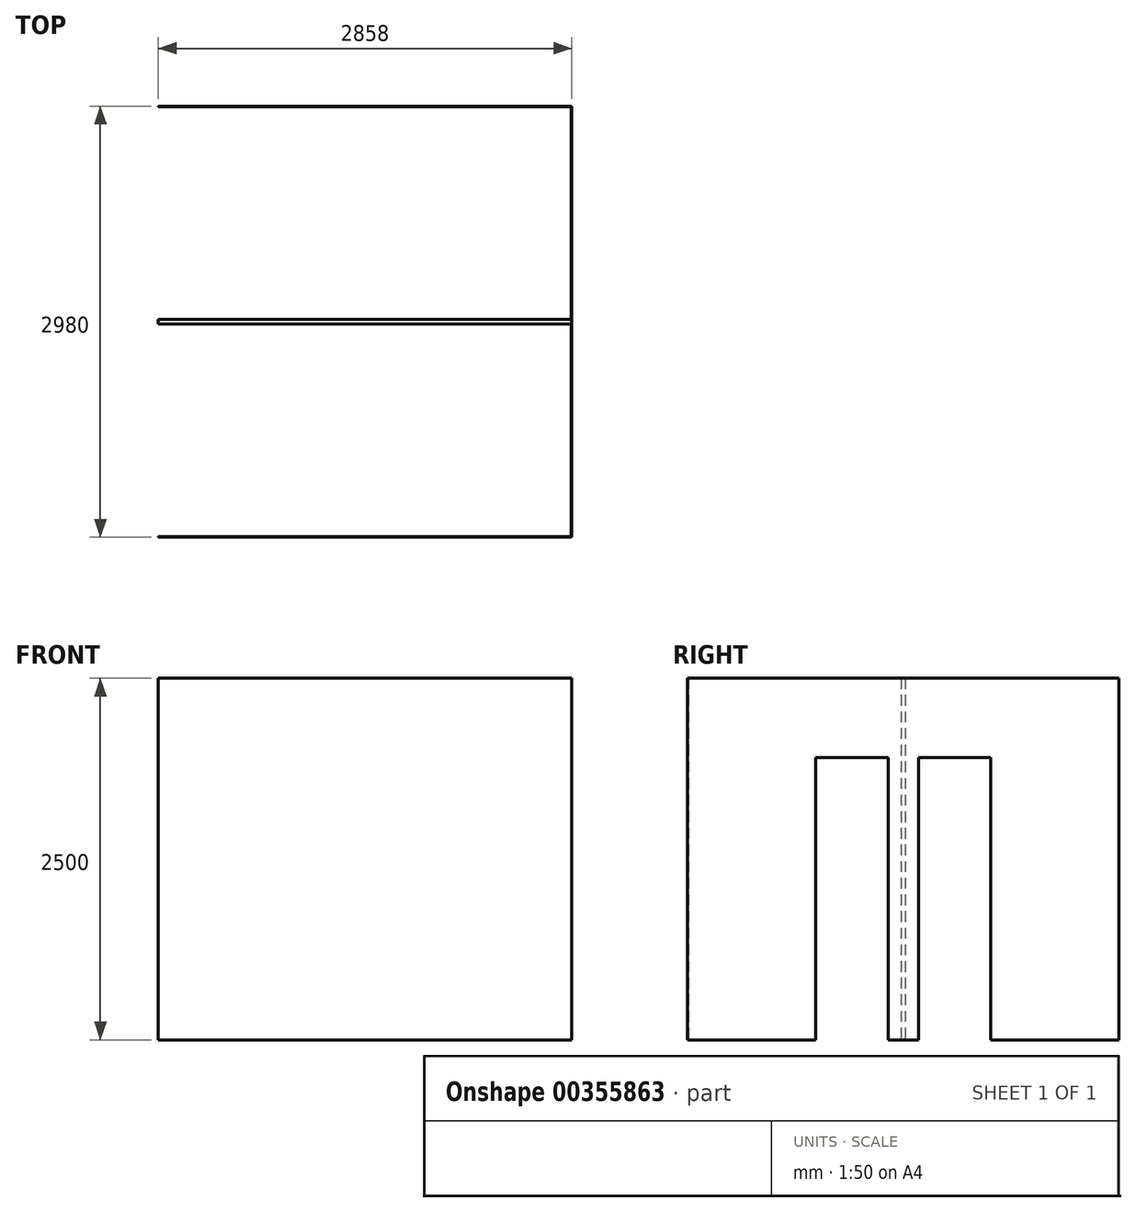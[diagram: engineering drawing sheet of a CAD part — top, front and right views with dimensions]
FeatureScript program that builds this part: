
annotation { "Feature Type Name" : "Feature", "Feature Type Description" : "" }
export const myFeature = defineFeature(function(context is Context, id is Id, definition is map)
    precondition{}
    {
        {
            var Q0;
            Q0=qCreatedBy(makeId("Top.planeOp"),FACE);
            var sketch = newSketch(context, id + "F0", { "sketchPlane" : qUnion([Q0])});
            skLineSegment(sketch, "E0.top", {"start": v(8302.06, 5858.21) * mm, "end": v(5348.06, 5858.21) * mm});
            skLineSegment(sketch, "E1.trimOffspring", {"start": v(8302.06, 8838.21) * mm, "end": v(8302.06, 7358.21) * mm});
            skPoint(sketch, "E2.start.orphan", {"position": v(8302.06, 7348.21) * mm});
            skLineSegment(sketch, "E3.trimOffspring", {"start": v(8302.06, 7338.21) * mm, "end": v(8302.06, 5858.21) * mm});
            skPoint(sketch, "E4.orphan", {"position": v(5348.06, 8858.21) * mm});
            skPoint(sketch, "E5.orphan", {"position": v(5348.06, 8838.21) * mm});
            skLineSegment(sketch, "E6", {"start": v(8302.06, 8838.21) * mm, "end": v(5348.06, 8838.21) * mm});
            skPoint(sketch, "E7.orphan", {"position": v(5348.06, 5858.21) * mm});
            skLineSegment(sketch, "E8.0", {"start": v(8297.06, 8833.21) * mm, "end": v(5348.06, 8833.21) * mm});
            skLineSegment(sketch, "E8.1", {"start": v(8297.06, 8833.21) * mm, "end": v(8297.06, 7363.21) * mm});
            skLineSegment(sketch, "E8.2", {"start": v(8297.06, 7363.21) * mm, "end": v(5343.06, 7363.21) * mm});
            skLineSegment(sketch, "E8.3", {"start": v(8297.06, 5863.21) * mm, "end": v(5348.06, 5863.21) * mm});
            skLineSegment(sketch, "E8.4", {"start": v(8297.06, 7333.21) * mm, "end": v(8297.06, 5863.21) * mm});
            skLineSegment(sketch, "E8.5", {"start": v(8297.06, 7333.21) * mm, "end": v(5343.06, 7333.21) * mm});
            skLineSegment(sketch, "E8.6", {"start": v(5343.06, 7363.21) * mm, "end": v(5343.06, 7333.21) * mm});
            skLineSegment(sketch, "E9", {"start": v(5348.06, 8833.21) * mm, "end": v(5348.06, 8838.21) * mm});
            skLineSegment(sketch, "E10", {"start": v(5348.06, 5863.21) * mm, "end": v(5348.06, 5858.21) * mm});
            skLineSegment(sketch, "E11", {"start": v(8302.06, 7358.21) * mm, "end": v(8302.06, 7338.21) * mm});
            skSolve(sketch);
        }
        {
            var Q0;
            Q0=qSketchRegion(id+"F0",true);
            extrude(context, id + "F1", {"entities" : qUnion([Q0]), "depth" : 2500 * mm});
        }
        {
            var Q0;
            Q0=makeQuery(id+"F1.opExtrude","SWEPT_FACE",FACE,{"disambiguationData":[OSD([sQuery(id+"F0.wireOp",EDGE,"E8.1")])]});
            var sketch = newSketch(context, id + "F2", { "sketchPlane" : qUnion([Q0])});
            skLineSegment(sketch, "E12.bottom", {"start": v(-7453.21, 1950) * mm, "end": v(-7953.21, 1950) * mm});
            skLineSegment(sketch, "E12.top", {"start": v(-7453.21, 0) * mm, "end": v(-7953.21, 0) * mm});
            skLineSegment(sketch, "E12.left", {"start": v(-7453.21, 1950) * mm, "end": v(-7453.21, 0) * mm});
            skLineSegment(sketch, "E12.right", {"start": v(-7953.21, 1950) * mm, "end": v(-7953.21, 0) * mm});
            skLineSegment(sketch, "E13.0", {"start": v(-7333.21, 2500) * mm, "end": v(-7333.21, 0) * mm});
            skLineSegment(sketch, "E14", {"start": v(-7348.21, 1595.6) * mm, "end": v(-7348.21, 1689.33) * mm});
            skPoint(sketch, "E15.end.orphan", {"position": v(-7453.21, 1595.6) * mm});
            skPoint(sketch, "E16.orphan", {"position": v(-7363.21, 1595.6) * mm});
            skPoint(sketch, "E17.end.orphan", {"position": v(-7333.21, 1595.6) * mm});
            skLineSegment(sketch, "E18.MirrorCS", {"start": v(-7243.21, 1950) * mm, "end": v(-7243.21, 0) * mm});
            skLineSegment(sketch, "E19.MirrorCS", {"start": v(-7243.21, 1950) * mm, "end": v(-6743.21, 1950) * mm});
            skLineSegment(sketch, "E20.MirrorCS", {"start": v(-6743.21, 1950) * mm, "end": v(-6743.21, 0) * mm});
            skLineSegment(sketch, "E21.MirrorCS", {"start": v(-7243.21, 0) * mm, "end": v(-6743.21, 0) * mm});
            skSolve(sketch);
        }
        {
            var Q0;
            Q0=qSketchRegion(id+"F2",true);
            extrude(context, id + "F3", {"entities" : qUnion([Q0]), "operationType" : NewBodyOperationType.REMOVE, "oppositeDirection" : true, "depth" : 300 * mm});
        }
        {
            var Q0;
            Q0=makeQuery(id+"F1.opExtrude","SWEPT_FACE",FACE,{"disambiguationData":[OSD([sQuery(id+"F0.wireOp",EDGE,"E8.5")])]});
            var sketch = newSketch(context, id + "F4", { "sketchPlane" : qUnion([Q0])});
            skLineSegment(sketch, "E22.left", {"start": v(5343.06, 2500) * mm, "end": v(5343.06, 0) * mm});
            skLineSegment(sketch, "E22.right", {"start": v(5444.06, 2500) * mm, "end": v(5444.06, 0) * mm});
            skLineSegment(sketch, "E23", {"start": v(5444.06, 2500) * mm, "end": v(5343.06, 2500) * mm});
            skLineSegment(sketch, "E24", {"start": v(5444.06, 0) * mm, "end": v(5343.06, 0) * mm});
            skSolve(sketch);
        }
        {
            var Q0;
            Q0=qSketchRegion(id+"F4",true);
            extrude(context, id + "F5", {"entities" : qUnion([Q0]), "operationType" : NewBodyOperationType.REMOVE, "oppositeDirection" : true, "depth" : 460 * mm});
        }
        {
            var Q0;
            Q0=makeQuery(id+"F1.opExtrude","SWEPT_FACE",FACE,{"disambiguationData":[OSD([sQuery(id+"F0.wireOp",EDGE,"E0.top")])]});
            var sketch = newSketch(context, id + "F6", { "sketchPlane" : qUnion([Q0])});
            skLineSegment(sketch, "E25.0", {"start": v(5444.06, 2500) * mm, "end": v(5444.06, 0) * mm});
            skLineSegment(sketch, "E26", {"start": v(5444.06, 2500) * mm, "end": v(5444.06, 2649.64) * mm});
            skLineSegment(sketch, "E27", {"start": v(5444.06, 2649.64) * mm, "end": v(5038.32, 2649.64) * mm});
            skLineSegment(sketch, "E28", {"start": v(5038.32, 2649.64) * mm, "end": v(5038.32, -210.07) * mm});
            skLineSegment(sketch, "E29", {"start": v(5038.32, -210.07) * mm, "end": v(5444.06, -140.88) * mm});
            skLineSegment(sketch, "E30", {"start": v(5444.06, -140.88) * mm, "end": v(5444.06, 0) * mm});
            skSolve(sketch);
        }
        {
            var Q0;
            Q0=qSketchRegion(id+"F6",true);
            extrude(context, id + "F7", {"entities" : qUnion([Q0]), "operationType" : NewBodyOperationType.REMOVE, "oppositeDirection" : true, "depth" : 4630 * mm});
        }
    });
